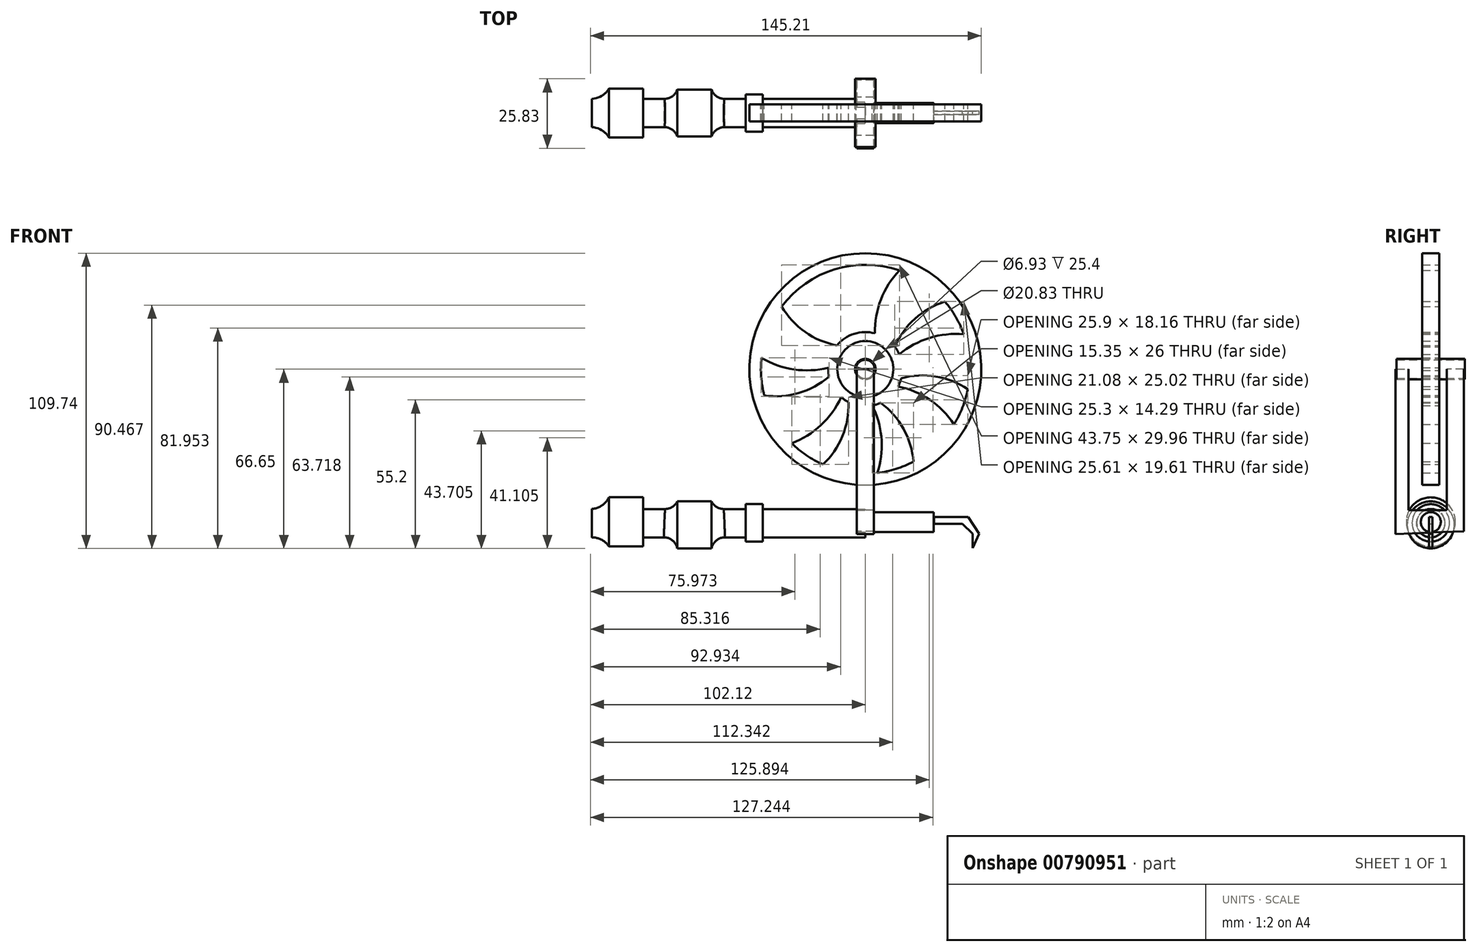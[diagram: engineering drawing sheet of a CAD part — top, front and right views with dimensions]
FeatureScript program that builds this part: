
annotation { "Feature Type Name" : "Feature", "Feature Type Description" : "" }
export const myFeature = defineFeature(function(context is Context, id is Id, definition is map)
    precondition{}
    {
        {
            var Q0;
            Q0=qCreatedBy(makeId("Front.planeOp"),FACE);
            var sketch = newSketch(context, id + "F0", { "sketchPlane" : qUnion([Q0])});
            skCircle(sketch, "E0", {"center": v(0, 0) * mm, "radius": 10.41 * mm});
            skArc(sketch, "E1", {"start": v(-1.85, 2.93) * mm, "mid": v(-2.94, 1.83) * mm, "end": v(-3.45, 0.38) * mm});
            skCircle(sketch, "E2", {"center": v(0, 0) * mm, "radius": 38.8 * mm});
            skArc(sketch, "E3", {"start": v(-5.15, 9.05) * mm, "mid": v(-5.63, 9.34) * mm, "end": v(-6.1, 9.64) * mm});
            skArc(sketch, "E4.1.1", {"start": v(3.58, 13.3) * mm, "mid": v(5.8, 25.9) * mm, "end": v(12.69, 36.67) * mm});
            skArc(sketch, "E4.2.1", {"start": v(12.63, 5.5) * mm, "mid": v(23.86, 11.61) * mm, "end": v(36.58, 12.94) * mm});
            skArc(sketch, "E4.3.1", {"start": v(12.17, -6.45) * mm, "mid": v(23.96, -11.41) * mm, "end": v(32.93, -20.53) * mm});
            skArc(sketch, "E4.4.1", {"start": v(2.55, -13.54) * mm, "mid": v(6.01, -25.85) * mm, "end": v(4.48, -38.54) * mm});
            skArc(sketch, "E4.5.1", {"start": v(-9, -10.43) * mm, "mid": v(-16.46, -20.82) * mm, "end": v(-27.34, -27.53) * mm});
            skArc(sketch, "E4.6.1", {"start": v(-10.29, 1.62) * mm, "mid": v(-10.82, 1.42) * mm, "end": v(-11.35, 1.24) * mm});
            skLineSegment(sketch, "E4.anchor1", {"start": v(0, 0) * mm, "end": v(-6.1, 9.64) * mm, "construction": true});
            skLineSegment(sketch, "E4.anchor2", {"start": v(0, 0) * mm, "end": v(-3.45, 0.38) * mm, "construction": true});
            skArc(sketch, "E5", {"start": v(0.32, 13.77) * mm, "mid": v(-3.15, 26.11) * mm, "end": v(-1.18, 38.78) * mm});
            skArc(sketch, "E6.1.0", {"start": v(-10.57, 8.84) * mm, "mid": v(-22.38, 13.82) * mm, "end": v(-31.06, 23.26) * mm});
            skArc(sketch, "E6.2.0", {"start": v(-13.5, -2.75) * mm, "mid": v(-24.76, -8.89) * mm, "end": v(-37.55, -9.79) * mm});
            skArc(sketch, "E6.3.0", {"start": v(-6.26, -12.27) * mm, "mid": v(-8.49, -24.9) * mm, "end": v(-15.76, -35.46) * mm});
            skArc(sketch, "E6.4.0", {"start": v(5.69, -12.55) * mm, "mid": v(14.17, -22.16) * mm, "end": v(17.9, -34.43) * mm});
            skArc(sketch, "E6.5.0", {"start": v(13.35, -3.38) * mm, "mid": v(26.16, -2.74) * mm, "end": v(38.08, -7.48) * mm});
            skArc(sketch, "E6.6.0", {"start": v(10.97, 8.33) * mm, "mid": v(18.45, 18.75) * mm, "end": v(29.58, 25.1) * mm});
            skCircle(sketch, "E7", {"center": v(0, 0) * mm, "radius": 43.09 * mm});
            skLineSegment(sketch, "E8.trimOffspring", {"start": v(-10.35, 1.13) * mm, "end": v(-11.35, 1.24) * mm, "construction": true});
            skCircle(sketch, "E9", {"center": v(0, 0) * mm, "radius": 13.78 * mm});
            skPoint(sketch, "E10.orphan", {"position": v(9.53, 4.2) * mm});
            skPoint(sketch, "E11.orphan", {"position": v(9.97, 3) * mm});
            skPoint(sketch, "E12.orphan", {"position": v(8.57, -5.92) * mm});
            skPoint(sketch, "E13.orphan", {"position": v(9.23, -4.82) * mm});
            skPoint(sketch, "E14.orphan", {"position": v(1.98, -10.22) * mm});
            skPoint(sketch, "E15.orphan", {"position": v(0.71, -10.39) * mm});
            skPoint(sketch, "E16.orphan", {"position": v(-6.76, -7.93) * mm});
            skPoint(sketch, "E17.orphan", {"position": v(-7.68, -7.04) * mm});
            skPoint(sketch, "E18.orphan", {"position": v(-10.4, 0.34) * mm});
            skArc(sketch, "E19.trimOffspring", {"start": v(-13.76, 0.53) * mm, "mid": v(-26.54, -0.11) * mm, "end": v(-38.57, 4.21) * mm});
            skPoint(sketch, "E20.orphan", {"position": v(-6.22, 8.35) * mm});
            skArc(sketch, "E21.trimOffspring", {"start": v(-8.17, 11.1) * mm, "mid": v(-16.63, 20.68) * mm, "end": v(-20.76, 32.78) * mm});
            skPoint(sketch, "E22.orphan", {"position": v(2.65, 10.07) * mm});
            skPoint(sketch, "E23.orphan", {"position": v(3.86, 9.67) * mm});
            skSolve(sketch);
        }
        {
            var Q0;
            Q0=qSketchRegion(id+"F0",true);
            var Q1;
            {var subQ0=sQuery(id+"F0.wireOp",EDGE,"E4.1.1");Q1=makeQuery(id+"F0.imprint","IMPRINT",FACE,{"disambiguationData":[TD([[makeQuery(id+"F0.imprint","IMPRINT",EDGE,{"derivedFrom":subQ0}),1.0]])]});}
            var Q2;
            {var subQ0=sQuery(id+"F0.wireOp",EDGE,"E4.2.1");Q2=makeQuery(id+"F0.imprint","IMPRINT",FACE,{"disambiguationData":[TD([[makeQuery(id+"F0.imprint","IMPRINT",EDGE,{"derivedFrom":subQ0}),1.0]])]});}
            var Q3;
            {var subQ0=sQuery(id+"F0.wireOp",EDGE,"E4.3.1");Q3=makeQuery(id+"F0.imprint","IMPRINT",FACE,{"disambiguationData":[TD([[makeQuery(id+"F0.imprint","IMPRINT",EDGE,{"derivedFrom":subQ0}),1.0]])]});}
            var Q4;
            {var subQ0=sQuery(id+"F0.wireOp",EDGE,"E4.4.1");Q4=makeQuery(id+"F0.imprint","IMPRINT",FACE,{"disambiguationData":[TD([[makeQuery(id+"F0.imprint","IMPRINT",EDGE,{"derivedFrom":subQ0}),1.0]])]});}
            var Q5;
            {var subQ0=sQuery(id+"F0.wireOp",EDGE,"E4.5.1");Q5=makeQuery(id+"F0.imprint","IMPRINT",FACE,{"disambiguationData":[TD([[makeQuery(id+"F0.imprint","IMPRINT",EDGE,{"derivedFrom":subQ0}),1.0]])]});}
            var Q6;
            {var subQ0=sQuery(id+"F0.wireOp",EDGE,"E6.2.0");Q6=makeQuery(id+"F0.imprint","IMPRINT",FACE,{"disambiguationData":[TD([[makeQuery(id+"F0.imprint","IMPRINT",EDGE,{"derivedFrom":subQ0}),-1.0]])]});}
            var Q7;
            {var subQ0=sQuery(id+"F0.wireOp",EDGE,"E6.1.0");Q7=makeQuery(id+"F0.imprint","IMPRINT",FACE,{"disambiguationData":[TD([[makeQuery(id+"F0.imprint","IMPRINT",EDGE,{"derivedFrom":subQ0}),-1.0]])]});}
            var Q8;
            {var subQ8=sQuery(id+"F0.wireOp",EDGE,"E0");var subQ9=makeQuery(id+"F0.imprint","IMPRINT",VERTEX,{"disambiguationData":[OD(0.0)],"derivedFrom":subQ8});Q8=makeQuery(id+"F0.imprint","IMPRINT",FACE,{"disambiguationData":[TD([[makeQuery(id+"F0.imprint","IMPRINT",EDGE,{"disambiguationData":[TD([[subQ9,-1.0]])],"derivedFrom":subQ8}),-1.0]])]});}
            var Q9;
            Q9=makeQuery(id+"F0.imprint","IMPRINT",FACE,{"disambiguationData":[TD([[makeQuery(id+"F0.imprint","IMPRINT",EDGE,{"derivedFrom":sQuery(id+"F0.wireOp",EDGE,"539e0326-62d8-41c1-9314-10fc468e663a")}),1.0]])]});
            extrude(context, id + "F1", {"entities" : qUnion([Q0, Q1, Q2, Q3, Q4, Q5, Q6, Q7, Q8, Q9]), "endBound" : BoundingType.SYMMETRIC, "depth" : 6.35 * mm, "offsetDistance" : 25.4 * mm});
        }
        {
            var Q0;
            Q0=qCreatedBy(makeId("Front.planeOp"),FACE);
            var sketch = newSketch(context, id + "F2", { "sketchPlane" : qUnion([Q0])});
            skCircle(sketch, "E24", {"center": v(0, 0) * mm, "radius": 3.47 * mm});
            skCircle(sketch, "E25", {"center": v(0, 0) * mm, "radius": 3.82 * mm});
            skSolve(sketch);
        }
        {
            var Q0;
            Q0=makeQuery(id+"F2.imprint","IMPRINT",FACE,{"disambiguationData":[TD([[makeQuery(id+"F2.imprint","IMPRINT",EDGE,{"derivedFrom":sQuery(id+"F2.wireOp",EDGE,"E24")}),-1.0]])]});
            extrude(context, id + "F3", {"entities" : qUnion([Q0]), "endBound" : BoundingType.SYMMETRIC, "depth" : 25.4 * mm, "offsetDistance" : 25.4 * mm});
        }
        {
            var Q0;
            Q0=qCreatedBy(makeId("Right.planeOp"),FACE);
            var sketch = newSketch(context, id + "F4", { "sketchPlane" : qUnion([Q0])});
            skPoint(sketch, "E26.start.orphan", {"position": v(-13.13, 0) * mm});
            skPoint(sketch, "E27.start.orphan", {"position": v(12.27, 0) * mm});
            skLineSegment(sketch, "E28", {"start": v(12.27, 0) * mm, "end": v(12.27, -60.25) * mm});
            skLineSegment(sketch, "E29", {"start": v(-13.13, 0) * mm, "end": v(-13.13, -61.26) * mm});
            skLineSegment(sketch, "E30", {"start": v(-13.13, -61.26) * mm, "end": v(12.27, -60.25) * mm});
            skLineSegment(sketch, "E31", {"start": v(-13.13, 0) * mm, "end": v(-8.3, 0) * mm});
            skLineSegment(sketch, "E32", {"start": v(-8.3, 0) * mm, "end": v(-8.3, -52.45) * mm});
            skLineSegment(sketch, "E33", {"start": v(-8.3, -52.45) * mm, "end": v(5.9, -52.45) * mm});
            skLineSegment(sketch, "E34", {"start": v(5.9, -52.45) * mm, "end": v(5.9, 0) * mm});
            skLineSegment(sketch, "E35", {"start": v(12.27, 0) * mm, "end": v(5.9, 0) * mm});
            skSolve(sketch);
        }
        {
            var Q0;
            Q0=qSketchRegion(id+"F4",true);
            extrude(context, id + "F5", {"entities" : qUnion([Q0]), "endBound" : BoundingType.SYMMETRIC, "depth" : 6.35 * mm, "offsetDistance" : 25.4 * mm});
        }
        {
            var Q0;
            Q0=qCreatedBy(makeId("Right.planeOp"),FACE);
            var sketch = newSketch(context, id + "F6", { "sketchPlane" : qUnion([Q0])});
            skCircle(sketch, "E36", {"center": v(0, -57.27) * mm, "radius": 5.28 * mm});
            skSolve(sketch);
        }
        {
            var Q0;
            Q0=qSketchRegion(id+"F6",true);
            extrude(context, id + "F7", {"entities" : qUnion([Q0]), "operationType" : NewBodyOperationType.ADD, "oppositeDirection" : true, "depth" : 101.6 * mm, "offsetDistance" : 25.4 * mm});
        }
        {
            var Q0;
            Q0=qCreatedBy(makeId("Right.planeOp"),FACE);
            cPlane(context, id + "F8", {"entities" : qUnion([Q0]), "cplaneType" : CPlaneType.OFFSET, "offset" : 38.1 * mm, "oppositeDirection" : true, "width" : 152.4 * mm, "height" : 152.4 * mm});
        }
        {
            var Q0;
            Q0=qCreatedBy(id+"F8.planeOp",FACE);
            var sketch = newSketch(context, id + "F9", { "sketchPlane" : qUnion([Q0])});
            skCircle(sketch, "E37", {"center": v(0, -57.15) * mm, "radius": 6.96 * mm});
            skSolve(sketch);
        }
        {
            var Q0;
            Q0=qSketchRegion(id+"F9",true);
            extrude(context, id + "F10", {"entities" : qUnion([Q0]), "operationType" : NewBodyOperationType.ADD, "oppositeDirection" : true, "depth" : 6.35 * mm, "offsetDistance" : 25.4 * mm});
        }
        {
            var Q0;
            Q0=qCreatedBy(id+"F8.planeOp",FACE);
            cPlane(context, id + "F11", {"entities" : qUnion([Q0]), "cplaneType" : CPlaneType.OFFSET, "offset" : 25.4 * mm, "oppositeDirection" : true, "width" : 152.4 * mm, "height" : 152.4 * mm});
        }
        {
            var Q0;
            Q0=qCreatedBy(id+"F11.planeOp",FACE);
            var sketch = newSketch(context, id + "F12", { "sketchPlane" : qUnion([Q0])});
            skCircle(sketch, "E38", {"center": v(0, -57.9) * mm, "radius": 8.75 * mm});
            skSolve(sketch);
        }
        {
            var Q0;
            Q0=qSketchRegion(id+"F12",true);
            extrude(context, id + "F13", {"entities" : qUnion([Q0]), "operationType" : NewBodyOperationType.ADD, "endBound" : BoundingType.SYMMETRIC, "depth" : 12.7 * mm, "offsetDistance" : 25.4 * mm});
        }
        {
            var Q0;
            {var subQ0=sQuery(id+"F6.wireOp",EDGE,"E36");Q0=makeQuery(id+"F13.boolean.opBoolean","INTERSECT",EDGE,{"derivedFrom":[makeQuery(id+"F10.boolean.opBoolean","SPLIT",FACE,{"disambiguationData":[TD([makeQuery(id+"F7.opExtrude","CAP_FACE",FACE,{"disambiguationData":[OSD([subQ0])],"isStart":false})])],"derivedFrom":makeQuery(id+"F7.opExtrude","SWEPT_FACE",FACE,{"disambiguationData":[OSD([subQ0])]})}),makeQuery(id+"F13.opExtrude","CAP_FACE",FACE,{"disambiguationData":[OSD([sQuery(id+"F12.wireOp",EDGE,"E38")])],"isStart":false})]});}
            var Q1;
            {var subQ0=sQuery(id+"F6.wireOp",EDGE,"E36");Q1=makeQuery(id+"F13.boolean.opBoolean","INTERSECT",EDGE,{"derivedFrom":[makeQuery(id+"F10.boolean.opBoolean","SPLIT",FACE,{"disambiguationData":[TD([makeQuery(id+"F7.opExtrude","CAP_FACE",FACE,{"disambiguationData":[OSD([subQ0])],"isStart":false})])],"derivedFrom":makeQuery(id+"F7.opExtrude","SWEPT_FACE",FACE,{"disambiguationData":[OSD([subQ0])]})}),makeQuery(id+"F13.opExtrude","CAP_FACE",FACE,{"disambiguationData":[OSD([sQuery(id+"F12.wireOp",EDGE,"E38")])],"isStart":true})]});}
            fillet(context, id + "F14", {"entities" : qUnion([Q0, Q1]), "radius" : 5.08 * mm, "tangentPropagation" : true, "allowEdgeOverflow" : false});
        }
        {
            var Q0;
            Q0=qCreatedBy(id+"F11.planeOp",FACE);
            cPlane(context, id + "F15", {"entities" : qUnion([Q0]), "cplaneType" : CPlaneType.OFFSET, "offset" : 25.4 * mm, "oppositeDirection" : true, "width" : 152.4 * mm, "height" : 152.4 * mm});
        }
        {
            var Q0;
            Q0=qCreatedBy(id+"F15.planeOp",FACE);
            var sketch = newSketch(context, id + "F16", { "sketchPlane" : qUnion([Q0])});
            skCircle(sketch, "E39", {"center": v(0, -56.78) * mm, "radius": 9.12 * mm});
            skSolve(sketch);
        }
        {
            var Q0;
            Q0=qSketchRegion(id+"F16",true);
            extrude(context, id + "F17", {"entities" : qUnion([Q0]), "operationType" : NewBodyOperationType.ADD, "endBound" : BoundingType.SYMMETRIC, "oppositeDirection" : true, "depth" : 12.7 * mm, "offsetDistance" : 25.4 * mm});
        }
        {
            var Q0;
            {var subQ0=sQuery(id+"F6.wireOp",EDGE,"E36");var subQ1=makeQuery(id+"F7.opExtrude","CAP_FACE",FACE,{"disambiguationData":[OSD([subQ0])],"isStart":false});Q0=makeQuery(id+"F17.boolean.opBoolean","INTERSECT",EDGE,{"derivedFrom":[makeQuery(id+"F13.boolean.opBoolean","SPLIT",FACE,{"disambiguationData":[TD([subQ1])],"derivedFrom":makeQuery(id+"F10.boolean.opBoolean","SPLIT",FACE,{"disambiguationData":[TD([subQ1])],"derivedFrom":makeQuery(id+"F7.opExtrude","SWEPT_FACE",FACE,{"disambiguationData":[OSD([subQ0])]})})}),makeQuery(id+"F17.opExtrude","CAP_FACE",FACE,{"disambiguationData":[OSD([sQuery(id+"F16.wireOp",EDGE,"E39")])],"isStart":false})]});}
            fillet(context, id + "F18", {"entities" : qUnion([Q0]), "radius" : 7.62 * mm, "tangentPropagation" : true, "allowEdgeOverflow" : false});
        }
        {
            var Q0;
            Q0=qCreatedBy(makeId("Right.planeOp"),FACE);
            var sketch = newSketch(context, id + "F19", { "sketchPlane" : qUnion([Q0])});
            skCircle(sketch, "E40", {"center": v(0, -56.85) * mm, "radius": 3.72 * mm});
            skSolve(sketch);
        }
        {
            var Q0;
            Q0=qSketchRegion(id+"F19",true);
            extrude(context, id + "F20", {"entities" : qUnion([Q0]), "operationType" : NewBodyOperationType.ADD, "depth" : 25.4 * mm, "offsetDistance" : 25.4 * mm});
        }
        {
            var Q0;
            Q0=qCreatedBy(makeId("Front.planeOp"),FACE);
            var sketch = newSketch(context, id + "F21", { "sketchPlane" : qUnion([Q0])});
            skLineSegment(sketch, "E41", {"start": v(25.48, -54.99) * mm, "end": v(38.25, -54.99) * mm});
            skLineSegment(sketch, "E42", {"start": v(38.25, -54.99) * mm, "end": v(42.29, -61.2) * mm});
            skLineSegment(sketch, "E43", {"start": v(42.29, -61.2) * mm, "end": v(39.9, -66.47) * mm});
            skLineSegment(sketch, "E44", {"start": v(39.9, -66.47) * mm, "end": v(39.9, -61.16) * mm});
            skLineSegment(sketch, "E45", {"start": v(39.9, -61.16) * mm, "end": v(36.07, -57.52) * mm});
            skLineSegment(sketch, "E46", {"start": v(36.07, -57.52) * mm, "end": v(25.46, -57.52) * mm});
            skLineSegment(sketch, "E47", {"start": v(25.46, -57.52) * mm, "end": v(25.48, -54.99) * mm});
            skSolve(sketch);
        }
        {
            var Q0;
            Q0=makeQuery(id+"F21.imprint","IMPRINT",FACE,{"disambiguationData":[TD([[makeQuery(id+"F21.imprint","IMPRINT",EDGE,{"derivedFrom":sQuery(id+"F21.wireOp",EDGE,"E41")}),-1.0]])]});
            extrude(context, id + "F22", {"entities" : qUnion([Q0]), "endBound" : BoundingType.SYMMETRIC, "depth" : 1.27 * mm, "offsetDistance" : 25.4 * mm});
        }
    });
